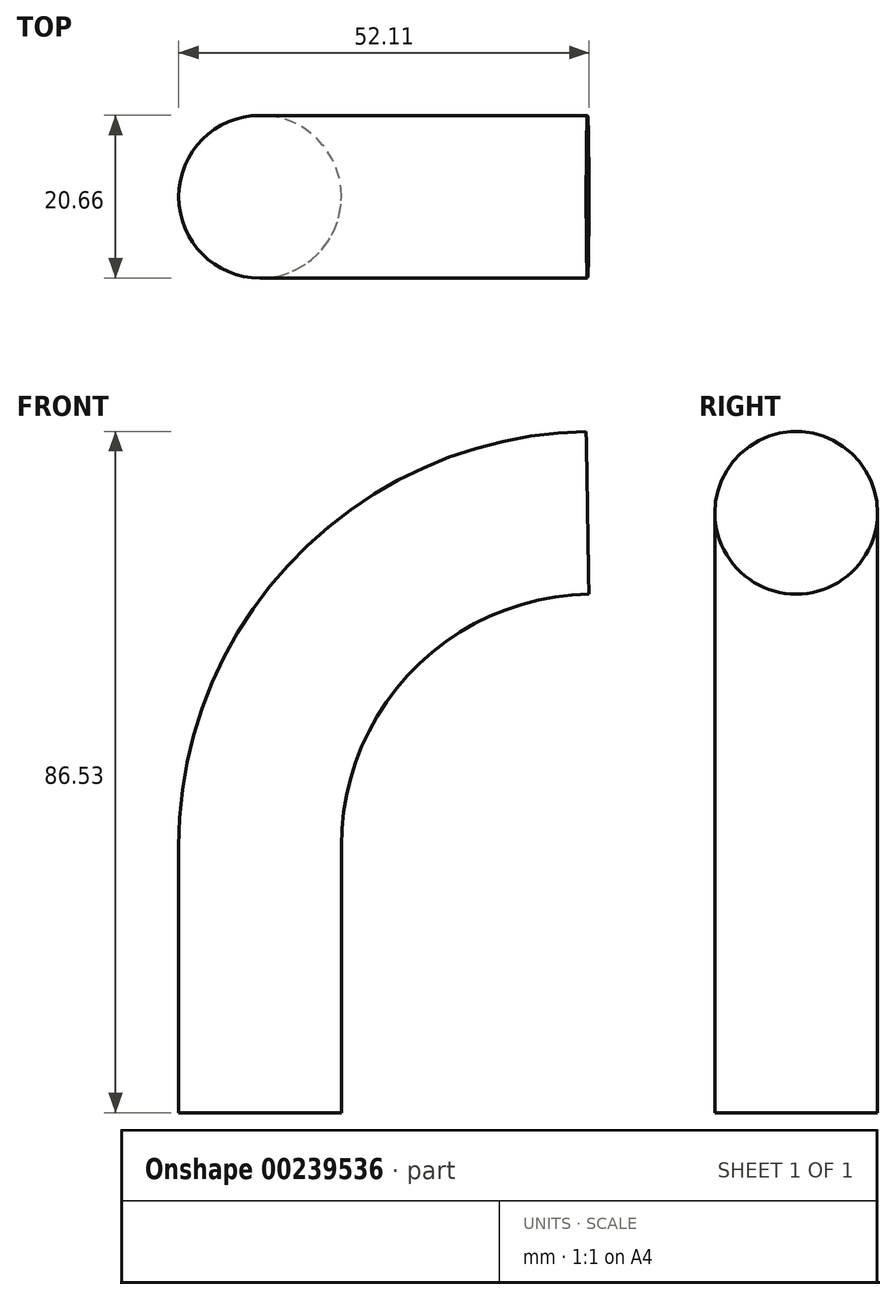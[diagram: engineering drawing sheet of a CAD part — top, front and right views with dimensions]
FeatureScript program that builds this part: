
annotation { "Feature Type Name" : "Feature", "Feature Type Description" : "" }
export const myFeature = defineFeature(function(context is Context, id is Id, definition is map)
    precondition{}
    {
        {
            var Q0;
            Q0=qCreatedBy(makeId("Front.planeOp"),FACE);
            var sketch = newSketch(context, id + "F0", { "sketchPlane" : qUnion([Q0])});
            skLineSegment(sketch, "E0", {"start": v(0, 0) * mm, "end": v(0, 33.88) * mm});
            skArc(sketch, "E1", {"start": v(41.6, 76.2) * mm, "mid": v(12.14, 63.55) * mm, "end": v(0, 33.88) * mm});
            skSolve(sketch);
        }
        {
            var Q0;
            Q0=qCreatedBy(makeId("Top.planeOp"),FACE);
            var sketch = newSketch(context, id + "F1", { "sketchPlane" : qUnion([Q0])});
            skCircle(sketch, "E2", {"center": v(0, 0) * mm, "radius": 10.33 * mm});
            skSolve(sketch);
        }
        {
            var Q0;
            Q0 = qSketchRegion(id + "F1", true);
            var Q1;
            Q1=sQuery(id+"F0.wireOp",EDGE,"E0");
            var Q2;
            Q2=sQuery(id+"F0.wireOp",EDGE,"E1");
            sweep(context, id + "F2", {"profiles" : qUnion([Q0]), "path" : qUnion([Q1, Q2])});
        }
    });
